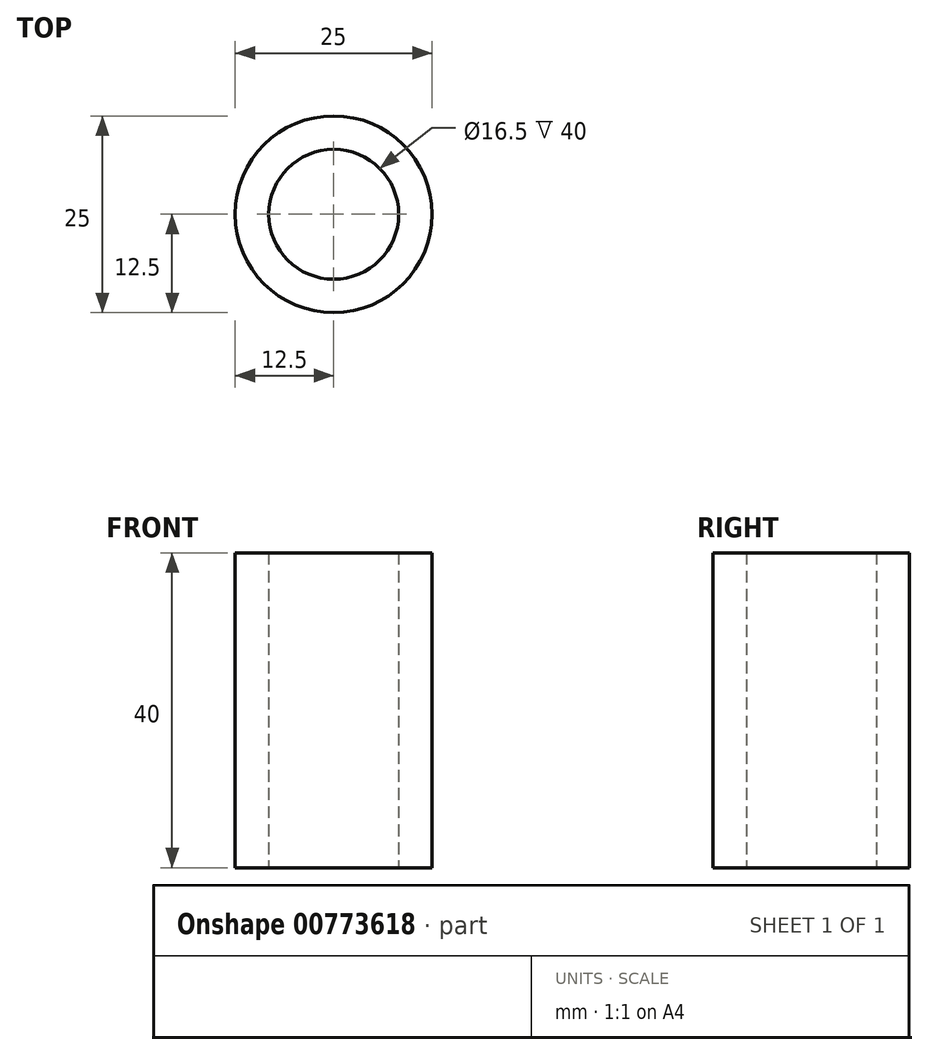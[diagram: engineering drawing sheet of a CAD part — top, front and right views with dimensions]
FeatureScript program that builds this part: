
annotation { "Feature Type Name" : "Feature", "Feature Type Description" : "" }
export const myFeature = defineFeature(function(context is Context, id is Id, definition is map)
    precondition{}
    {
        {
            var Q0;
            Q0=qCreatedBy(makeId("Top.planeOp"),FACE);
            var sketch = newSketch(context, id + "F0", { "sketchPlane" : qUnion([Q0])});
            skCircle(sketch, "E0", {"center": v(0, 0) * mm, "radius": 8.25 * mm});
            skCircle(sketch, "E1", {"center": v(0, 0) * mm, "radius": 12.5 * mm});
            skSolve(sketch);
        }
        {
            var Q0;
            Q0=makeQuery(id+"F0.imprint","IMPRINT",FACE,{"disambiguationData":[TD([[makeQuery(id+"F0.imprint","IMPRINT",EDGE,{"derivedFrom":sQuery(id+"F0.wireOp",EDGE,"E0")}),-1.0]])]});
            extrude(context, id + "F1", {"entities" : qUnion([Q0]), "depth" : 40 * mm, "offsetDistance" : 25 * mm});
        }
    });
